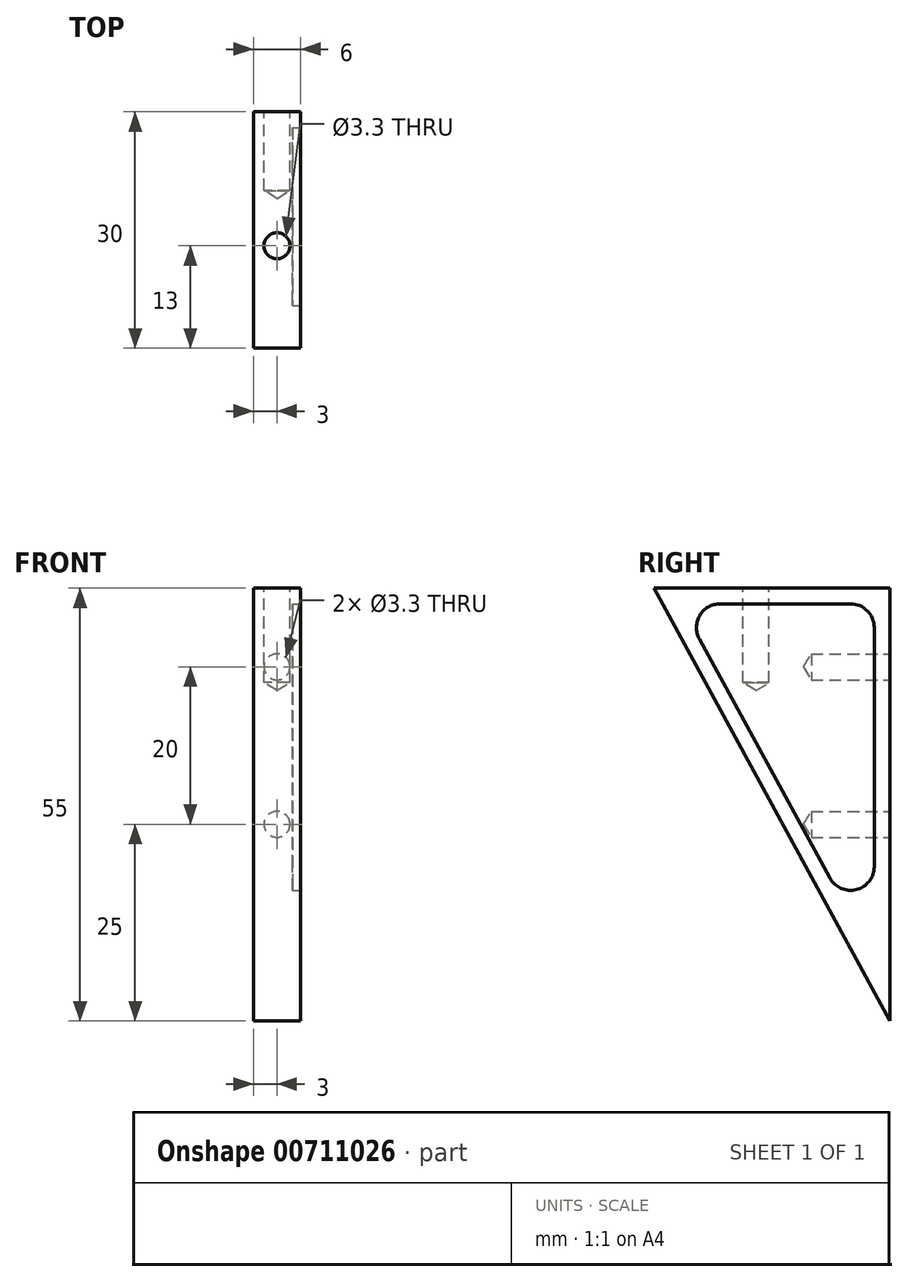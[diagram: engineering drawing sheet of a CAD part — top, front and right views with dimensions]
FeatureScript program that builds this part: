
annotation { "Feature Type Name" : "Feature", "Feature Type Description" : "" }
export const myFeature = defineFeature(function(context is Context, id is Id, definition is map)
    precondition{}
    {
        {
            var Q0;
            Q0=qCreatedBy(makeId("Right.planeOp"),FACE);
            var sketch = newSketch(context, id + "F0", { "sketchPlane" : qUnion([Q0])});
            skLineSegment(sketch, "E0", {"start": v(0, 0) * mm, "end": v(0, -55) * mm});
            skLineSegment(sketch, "E1", {"start": v(0, -55) * mm, "end": v(-30, 0) * mm});
            skLineSegment(sketch, "E2", {"start": v(-30, 0) * mm, "end": v(0, 0) * mm});
            skSolve(sketch);
        }
        {
            var Q0;
            Q0=makeQuery(id+"F0.imprint","IMPRINT",FACE,{"disambiguationData":[TD([[makeQuery(id+"F0.imprint","IMPRINT",EDGE,{"derivedFrom":sQuery(id+"F0.wireOp",EDGE,"E0")}),-1.0]])]});
            extrude(context, id + "F1", {"entities" : qUnion([Q0]), "endBound" : BoundingType.SYMMETRIC, "depth" : 6 * mm, "offsetDistance" : 25 * mm});
        }
        {
            var Q0;
            Q0=makeQuery(id+"F1.opExtrude","SWEPT_FACE",FACE,{"disambiguationData":[OSD([sQuery(id+"F0.wireOp",EDGE,"E0")])]});
            var sketch = newSketch(context, id + "F2", { "sketchPlane" : qUnion([Q0])});
            skPoint(sketch, "E3", {"position": v(0, -10) * mm});
            skPoint(sketch, "E4", {"position": v(0, -30) * mm});
            skSolve(sketch);
        }
        {
            var Q0;
            Q0=sQuery(id+"F2.wireOp",VERTEX,"E3");
            var Q1;
            Q1=sQuery(id+"F2.wireOp",VERTEX,"E4");
            var Q2;
            Q2=makeQuery(id+"F1.opExtrude","SWEPT_BODY",BODY,{"disambiguationData":[OSD([sQuery(id+"F0.wireOp",EDGE,"E0"),sQuery(id+"F0.wireOp",EDGE,"E1"),sQuery(id+"F0.wireOp",EDGE,"E2")])]});
            hole(context, id + "F3", {"style" : HoleStyle.SIMPLE, "endStyle" : HoleEndStyle.BLIND, "standardTappedOrClearance" : lookupTablePath({ "standard" : "ISO", "engagement" : "75%", "pitch" : "0.7 mm", "size" : "M4", "type" : "Tapped" }), "standardBlindInLast" : lookupTablePath({ "standard" : "ISO", "engagement" : "75%", "pitch" : "0.7 mm", "size" : "M4", "type" : "Tapped" }), "holeDiameter" : 3.3 * mm, "majorDiameter" : 4 * mm, "showTappedDepth" : true, "holeDepth" : 10 * mm, "tappedDepth" : 7.9 * mm, "tapClearance" : 3, "startFromSketch" : true, "locations" : qUnion([Q0, Q1]), "scope" : qUnion([Q2])});
        }
        {
            var Q0;
            Q0=makeQuery(id+"F1.opExtrude","SWEPT_FACE",FACE,{"disambiguationData":[OSD([sQuery(id+"F0.wireOp",EDGE,"E2")])]});
            var sketch = newSketch(context, id + "F4", { "sketchPlane" : qUnion([Q0])});
            skPoint(sketch, "E5", {"position": v(0, -17) * mm});
            skSolve(sketch);
        }
        {
            var Q0;
            Q0=sQuery(id+"F4.wireOp",VERTEX,"8912a393-99c2-45ca-b2c4-6134073d903a");
            var Q1;
            Q1=sQuery(id+"F4.wireOp",VERTEX,"E5");
            var Q2;
            Q2=makeQuery(id+"F1.opExtrude","SWEPT_BODY",BODY,{"disambiguationData":[OSD([sQuery(id+"F0.wireOp",EDGE,"E0"),sQuery(id+"F0.wireOp",EDGE,"E1"),sQuery(id+"F0.wireOp",EDGE,"E2")])]});
            hole(context, id + "F5", {"style" : HoleStyle.SIMPLE, "endStyle" : HoleEndStyle.BLIND, "standardTappedOrClearance" : lookupTablePath({ "standard" : "ISO", "engagement" : "75%", "pitch" : "0.7 mm", "size" : "M4", "type" : "Tapped" }), "standardBlindInLast" : lookupTablePath({ "standard" : "ISO", "engagement" : "75%", "pitch" : "0.7 mm", "size" : "M4", "type" : "Tapped" }), "holeDiameter" : 3.3 * mm, "majorDiameter" : 4 * mm, "showTappedDepth" : true, "holeDepth" : 12 * mm, "tappedDepth" : 9.9 * mm, "tapClearance" : 3, "startFromSketch" : true, "locations" : qUnion([Q0, Q1]), "scope" : qUnion([Q2])});
        }
        {
            var Q0;
            Q0=makeQuery(id+"F1.opExtrude","CAP_FACE",FACE,{"disambiguationData":[OSD([sQuery(id+"F0.wireOp",EDGE,"E0"),sQuery(id+"F0.wireOp",EDGE,"E1"),sQuery(id+"F0.wireOp",EDGE,"E2")])],"isStart":false});
            var sketch = newSketch(context, id + "F6", { "sketchPlane" : qUnion([Q0])});
            skLineSegment(sketch, "E6.0.0", {"start": v(0, 0) * mm, "end": v(-30, 0) * mm});
            skLineSegment(sketch, "E6.0.1", {"start": v(-30, 0) * mm, "end": v(0, -55) * mm});
            skLineSegment(sketch, "E6.0.2", {"start": v(0, -55) * mm, "end": v(0, 0) * mm});
            skLineSegment(sketch, "E7.0", {"start": v(-5, -2) * mm, "end": v(-21.58, -2) * mm});
            skLineSegment(sketch, "E7.1", {"start": v(-2, -35.4) * mm, "end": v(-2, -5) * mm});
            skLineSegment(sketch, "E7.2", {"start": v(-24.21, -6.44) * mm, "end": v(-7.63, -36.83) * mm});
            skPoint(sketch, "E8.visualSharp", {"position": v(-26.63, -2) * mm});
            skArc(sketch, "E8.filletArc", {"start": v(-21.58, -2) * mm, "mid": v(-24.16, -3.47) * mm, "end": v(-24.21, -6.44) * mm});
            skPoint(sketch, "E9.visualSharp", {"position": v(-2, -2) * mm});
            skArc(sketch, "E9.filletArc", {"start": v(-2, -5) * mm, "mid": v(-2.88, -2.88) * mm, "end": v(-5, -2) * mm});
            skPoint(sketch, "E10.visualSharp", {"position": v(-2, -47.16) * mm});
            skArc(sketch, "E10.filletArc", {"start": v(-7.63, -36.83) * mm, "mid": v(-4.26, -38.3) * mm, "end": v(-2, -35.4) * mm});
            skSolve(sketch);
        }
        {
            var Q0;
            Q0=makeQuery(id+"F6.imprint","IMPRINT",FACE,{"disambiguationData":[TD([[makeQuery(id+"F6.imprint","IMPRINT",EDGE,{"derivedFrom":sQuery(id+"F6.wireOp",EDGE,"E7.0")}),1.0]])]});
            extrude(context, id + "F7", {"entities" : qUnion([Q0]), "operationType" : NewBodyOperationType.REMOVE, "oppositeDirection" : true, "depth" : 1 * mm, "offsetDistance" : 25 * mm});
        }
    });
